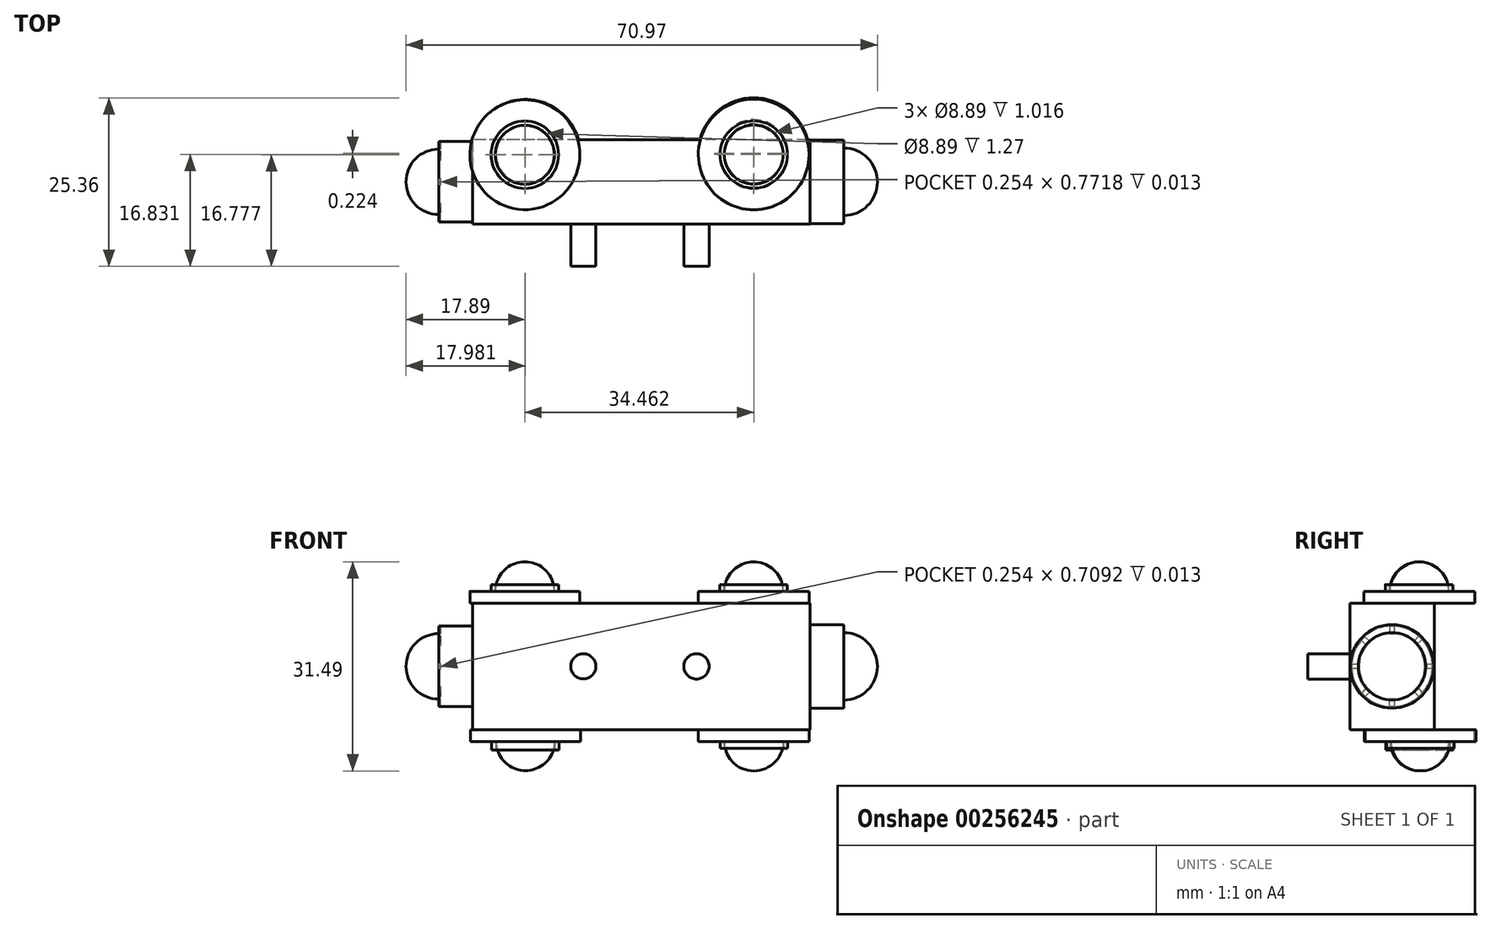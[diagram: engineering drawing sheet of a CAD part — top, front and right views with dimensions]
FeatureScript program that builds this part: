
annotation { "Feature Type Name" : "Feature", "Feature Type Description" : "" }
export const myFeature = defineFeature(function(context is Context, id is Id, definition is map)
    precondition{}
    {
        {
            var Q0;
            Q0=qCreatedBy(makeId("Front.planeOp"),FACE);
            var sketch = newSketch(context, id + "F0", { "sketchPlane" : qUnion([Q0])});
            skLineSegment(sketch, "E0.bottom", {"start": v(25.4, 9.53) * mm, "end": v(-25.4, 9.53) * mm});
            skLineSegment(sketch, "E0.top", {"start": v(25.4, -9.52) * mm, "end": v(-25.4, -9.52) * mm});
            skLineSegment(sketch, "E0.left", {"start": v(25.4, 9.53) * mm, "end": v(25.4, -9.53) * mm});
            skLineSegment(sketch, "E0.right", {"start": v(-25.4, 9.53) * mm, "end": v(-25.4, -9.52) * mm});
            skPoint(sketch, "E0.middle", {"position": v(0, 0) * mm});
            skSolve(sketch);
        }
        {
            var Q0;
            Q0 = qSketchRegion(id + "F0", true);
            extrude(context, id + "F1", {"entities" : qUnion([Q0]), "endBound" : BoundingType.SYMMETRIC, "depth" : 12.7 * mm});
        }
        {
            var Q0;
            Q0=makeQuery(id+"F1.opExtrude","CAP_FACE",FACE,{"disambiguationData":[OSD([sQuery(id+"F0.wireOp",EDGE,"E0.bottom"),sQuery(id+"F0.wireOp",EDGE,"E0.top"),sQuery(id+"F0.wireOp",EDGE,"E0.left"),sQuery(id+"F0.wireOp",EDGE,"E0.right")])],"isStart":false});
            var sketch = newSketch(context, id + "F2", { "sketchPlane" : qUnion([Q0])});
            skCircle(sketch, "E1", {"center": v(-8.72, 0) * mm, "radius": 1.89 * mm});
            skSolve(sketch);
        }
        {
            var Q0;
            Q0 = qSketchRegion(id + "F2", true);
            extrude(context, id + "F3", {"entities" : qUnion([Q0]), "operationType" : NewBodyOperationType.ADD, "depth" : 6.35 * mm});
        }
        {
            var Q0;
            Q0=makeQuery(id+"F1.opExtrude","CAP_FACE",FACE,{"disambiguationData":[OSD([sQuery(id+"F0.wireOp",EDGE,"E0.bottom"),sQuery(id+"F0.wireOp",EDGE,"E0.top"),sQuery(id+"F0.wireOp",EDGE,"E0.left"),sQuery(id+"F0.wireOp",EDGE,"E0.right")])],"isStart":false});
            var sketch = newSketch(context, id + "F4", { "sketchPlane" : qUnion([Q0])});
            skCircle(sketch, "E2", {"center": v(8.31, 0) * mm, "radius": 1.9 * mm});
            skSolve(sketch);
        }
        {
            var Q0;
            Q0 = qSketchRegion(id + "F4", true);
            extrude(context, id + "F5", {"entities" : qUnion([Q0]), "operationType" : NewBodyOperationType.ADD, "depth" : 6.35 * mm});
        }
        {
            var Q0;
            Q0=makeQuery(id+"F1.opExtrude","SWEPT_FACE",FACE,{"disambiguationData":[OSD([sQuery(id+"F0.wireOp",EDGE,"E0.left")])]});
            var sketch = newSketch(context, id + "F6", { "sketchPlane" : qUnion([Q0])});
            skCircle(sketch, "E3", {"center": v(0, 0) * mm, "radius": 6.28 * mm});
            skSolve(sketch);
        }
        {
            var Q0;
            Q0 = qSketchRegion(id + "F6", true);
            extrude(context, id + "F7", {"entities" : qUnion([Q0]), "operationType" : NewBodyOperationType.ADD, "depth" : 5.08 * mm});
        }
        {
            var Q0;
            Q0=makeQuery(id+"F7.opExtrude","CAP_FACE",FACE,{"disambiguationData":[OSD([sQuery(id+"F6.wireOp",EDGE,"E3")])],"isStart":false});
            var sketch = newSketch(context, id + "F8", { "sketchPlane" : qUnion([Q0])});
            skArc(sketch, "E4", {"start": v(5.08, 0) * mm, "mid": v(0, 5.08) * mm, "end": v(-5.08, 0) * mm});
            skLineSegment(sketch, "E5", {"start": v(-5.08, 0) * mm, "end": v(5.08, 0) * mm});
            skSolve(sketch);
        }
        {
            var Q0;
            Q0 = qSketchRegion(id + "F8", true);
            var Q1;
            Q1=sQuery(id+"F8.wireOp",EDGE,"E5");
            revolve(context, id + "F9", {"operationType" : NewBodyOperationType.ADD, "entities" : qUnion([Q0]), "axis" : qUnion([Q1]), "revolveType" : RevolveType.ONE_DIRECTION, "angle" : 180 * degree});
        }
        {
            var Q0;
            Q0=makeQuery(id+"F1.opExtrude","SWEPT_FACE",FACE,{"disambiguationData":[OSD([sQuery(id+"F0.wireOp",EDGE,"E0.right")])]});
            var sketch = newSketch(context, id + "F10", { "sketchPlane" : qUnion([Q0])});
            skCircle(sketch, "E6", {"center": v(0, 0) * mm, "radius": 6.07 * mm});
            skSolve(sketch);
        }
        {
            var Q0;
            Q0 = qSketchRegion(id + "F10", true);
            extrude(context, id + "F11", {"entities" : qUnion([Q0]), "operationType" : NewBodyOperationType.ADD, "depth" : 5.08 * mm});
        }
        {
            var Q0;
            Q0=makeQuery(id+"F11.opExtrude","CAP_FACE",FACE,{"disambiguationData":[OSD([sQuery(id+"F10.wireOp",EDGE,"E6")])],"isStart":false});
            var sketch = newSketch(context, id + "F12", { "sketchPlane" : qUnion([Q0])});
            skArc(sketch, "E7", {"start": v(-4.93, 0) * mm, "mid": v(0, -4.93) * mm, "end": v(4.93, 0) * mm});
            skLineSegment(sketch, "E8", {"start": v(4.93, 0) * mm, "end": v(-4.93, 0) * mm});
            skSolve(sketch);
        }
        {
            var Q0;
            Q0 = qSketchRegion(id + "F12", true);
            var Q1;
            Q1=sQuery(id+"F12.wireOp",EDGE,"E8");
            revolve(context, id + "F13", {"operationType" : NewBodyOperationType.ADD, "entities" : qUnion([Q0]), "axis" : qUnion([Q1]), "revolveType" : RevolveType.ONE_DIRECTION, "angle" : 180 * degree});
        }
        {
            var Q0;
            Q0=makeQuery(id+"F1.opExtrude","SWEPT_FACE",FACE,{"disambiguationData":[OSD([sQuery(id+"F0.wireOp",EDGE,"E0.top")])]});
            var sketch = newSketch(context, id + "F14", { "sketchPlane" : qUnion([Q0])});
            skCircle(sketch, "E9", {"center": v(-17.43, -4.13) * mm, "radius": 8.28 * mm});
            skSolve(sketch);
        }
        {
            var Q0;
            Q0 = qSketchRegion(id + "F14", true);
            extrude(context, id + "F15", {"entities" : qUnion([Q0]), "operationType" : NewBodyOperationType.ADD, "depth" : 1.78 * mm});
        }
        {
            var Q0;
            Q0=makeQuery(id+"F15.opExtrude","CAP_FACE",FACE,{"disambiguationData":[OSD([sQuery(id+"F14.wireOp",EDGE,"E9")])],"isStart":false});
            var sketch = newSketch(context, id + "F16", { "sketchPlane" : qUnion([Q0])});
            skCircle(sketch, "E10", {"center": v(-17.43, -4.13) * mm, "radius": 5.08 * mm});
            skSolve(sketch);
        }
        {
            var Q0;
            Q0 = qSketchRegion(id + "F16", true);
            extrude(context, id + "F17", {"entities" : qUnion([Q0]), "operationType" : NewBodyOperationType.ADD, "depth" : 1.27 * mm});
        }
        {
            var Q0;
            Q0=makeQuery(id+"F17.opExtrude","CAP_FACE",FACE,{"disambiguationData":[OSD([sQuery(id+"F16.wireOp",EDGE,"E10")])],"isStart":false});
            var sketch = newSketch(context, id + "F18", { "sketchPlane" : qUnion([Q0])});
            skCircle(sketch, "E11", {"center": v(-17.43, -4.13) * mm, "radius": 4.45 * mm});
            skSolve(sketch);
        }
        {
            var Q0;
            Q0 = qSketchRegion(id + "F18", true);
            extrude(context, id + "F19", {"entities" : qUnion([Q0]), "operationType" : NewBodyOperationType.REMOVE, "oppositeDirection" : true, "depth" : 1.27 * mm});
        }
        {
            var Q0;
            Q0=makeQuery(id+"F19.boolean.opBoolean","COPY",FACE,{"derivedFrom":makeQuery(id+"F19.opExtrude","CAP_FACE",FACE,{"disambiguationData":[OSD([sQuery(id+"F18.wireOp",EDGE,"E11")])],"isStart":false})});
            var sketch = newSketch(context, id + "F20", { "sketchPlane" : qUnion([Q0])});
            skArc(sketch, "E12", {"start": v(-17.43, -8.53) * mm, "mid": v(-13.03, -4.13) * mm, "end": v(-17.43, 0.27) * mm});
            skLineSegment(sketch, "E13", {"start": v(-17.43, -8.58) * mm, "end": v(-17.43, 0.31) * mm});
            skSolve(sketch);
        }
        {
            var Q0;
            Q0 = qSketchRegion(id + "F20", true);
            var Q1;
            Q1=sQuery(id+"F20.wireOp",EDGE,"E13");
            revolve(context, id + "F21", {"operationType" : NewBodyOperationType.ADD, "entities" : qUnion([Q0]), "axis" : qUnion([Q1]), "revolveType" : RevolveType.ONE_DIRECTION, "oppositeDirection" : true, "angle" : 180 * degree});
        }
        {
            var Q0;
            Q0=makeQuery(id+"F1.opExtrude","SWEPT_FACE",FACE,{"disambiguationData":[OSD([sQuery(id+"F0.wireOp",EDGE,"E0.top")])]});
            var sketch = newSketch(context, id + "F22", { "sketchPlane" : qUnion([Q0])});
            skCircle(sketch, "E14", {"center": v(16.94, -4.3) * mm, "radius": 8.36 * mm});
            skSolve(sketch);
        }
        {
            var Q0;
            Q0 = qSketchRegion(id + "F22", true);
            extrude(context, id + "F23", {"entities" : qUnion([Q0]), "operationType" : NewBodyOperationType.ADD, "depth" : 1.78 * mm});
        }
        {
            var Q0;
            Q0=makeQuery(id+"F23.opExtrude","CAP_FACE",FACE,{"disambiguationData":[OSD([sQuery(id+"F22.wireOp",EDGE,"E14")])],"isStart":false});
            var sketch = newSketch(context, id + "F24", { "sketchPlane" : qUnion([Q0])});
            skCircle(sketch, "E15", {"center": v(16.94, -4.3) * mm, "radius": 5.08 * mm});
            skSolve(sketch);
        }
        {
            var Q0;
            Q0 = qSketchRegion(id + "F24", true);
            extrude(context, id + "F25", {"entities" : qUnion([Q0]), "operationType" : NewBodyOperationType.ADD, "depth" : 1.02 * mm});
        }
        {
            var Q0;
            Q0=makeQuery(id+"F25.opExtrude","CAP_FACE",FACE,{"disambiguationData":[OSD([sQuery(id+"F24.wireOp",EDGE,"E15")])],"isStart":false});
            var sketch = newSketch(context, id + "F26", { "sketchPlane" : qUnion([Q0])});
            skCircle(sketch, "E16", {"center": v(16.94, -4.3) * mm, "radius": 4.45 * mm});
            skSolve(sketch);
        }
        {
            var Q0;
            Q0 = qSketchRegion(id + "F26", true);
            extrude(context, id + "F27", {"entities" : qUnion([Q0]), "operationType" : NewBodyOperationType.REMOVE, "oppositeDirection" : true, "depth" : 1.02 * mm});
        }
        {
            var Q0;
            Q0=makeQuery(id+"F27.boolean.opBoolean","COPY",FACE,{"derivedFrom":makeQuery(id+"F27.opExtrude","CAP_FACE",FACE,{"disambiguationData":[OSD([sQuery(id+"F26.wireOp",EDGE,"E16")])],"isStart":false})});
            var sketch = newSketch(context, id + "F28", { "sketchPlane" : qUnion([Q0])});
            skArc(sketch, "E17", {"start": v(16.95, -8.75) * mm, "mid": v(21.39, -4.3) * mm, "end": v(16.95, 0.14) * mm});
            skLineSegment(sketch, "E18", {"start": v(16.95, 0.14) * mm, "end": v(16.95, -8.75) * mm});
            skSolve(sketch);
        }
        {
            var Q0;
            Q0 = qSketchRegion(id + "F28", true);
            var Q1;
            Q1=sQuery(id+"F28.wireOp",EDGE,"E18");
            revolve(context, id + "F29", {"operationType" : NewBodyOperationType.ADD, "entities" : qUnion([Q0]), "axis" : qUnion([Q1]), "revolveType" : RevolveType.ONE_DIRECTION, "angle" : 180 * degree});
        }
        {
            var Q0;
            Q0=makeQuery(id+"F1.opExtrude","SWEPT_FACE",FACE,{"disambiguationData":[OSD([sQuery(id+"F0.wireOp",EDGE,"E0.bottom")])]});
            var sketch = newSketch(context, id + "F30", { "sketchPlane" : qUnion([Q0])});
            skCircle(sketch, "E19", {"center": v(16.93, 4.11) * mm, "radius": 8.33 * mm});
            skSolve(sketch);
        }
        {
            var Q0;
            Q0 = qSketchRegion(id + "F30", true);
            extrude(context, id + "F31", {"entities" : qUnion([Q0]), "operationType" : NewBodyOperationType.ADD, "depth" : 1.78 * mm});
        }
        {
            var Q0;
            Q0=makeQuery(id+"F31.opExtrude","CAP_FACE",FACE,{"disambiguationData":[OSD([sQuery(id+"F30.wireOp",EDGE,"E19")])],"isStart":false});
            var sketch = newSketch(context, id + "F32", { "sketchPlane" : qUnion([Q0])});
            skCircle(sketch, "E20", {"center": v(16.93, 4.11) * mm, "radius": 5.08 * mm});
            skSolve(sketch);
        }
        {
            var Q0;
            Q0 = qSketchRegion(id + "F32", true);
            extrude(context, id + "F33", {"entities" : qUnion([Q0]), "operationType" : NewBodyOperationType.ADD, "depth" : 1.02 * mm});
        }
        {
            var Q0;
            Q0=makeQuery(id+"F33.opExtrude","CAP_FACE",FACE,{"disambiguationData":[OSD([sQuery(id+"F32.wireOp",EDGE,"E20")])],"isStart":false});
            var sketch = newSketch(context, id + "F34", { "sketchPlane" : qUnion([Q0])});
            skCircle(sketch, "E21", {"center": v(16.93, 4.11) * mm, "radius": 4.44 * mm});
            skSolve(sketch);
        }
        {
            var Q0;
            Q0 = qSketchRegion(id + "F34", true);
            extrude(context, id + "F35", {"entities" : qUnion([Q0]), "operationType" : NewBodyOperationType.REMOVE, "oppositeDirection" : true, "depth" : 1.02 * mm});
        }
        {
            var Q0;
            Q0=makeQuery(id+"F35.boolean.opBoolean","COPY",FACE,{"derivedFrom":makeQuery(id+"F35.opExtrude","CAP_FACE",FACE,{"disambiguationData":[OSD([sQuery(id+"F34.wireOp",EDGE,"E21")])],"isStart":false})});
            var sketch = newSketch(context, id + "F36", { "sketchPlane" : qUnion([Q0])});
            skArc(sketch, "E22", {"start": v(16.93, 8.54) * mm, "mid": v(12.5, 4.11) * mm, "end": v(16.93, -0.32) * mm});
            skLineSegment(sketch, "E23", {"start": v(16.93, 8.56) * mm, "end": v(16.93, -0.33) * mm});
            skSolve(sketch);
        }
        {
            var Q0;
            Q0 = qSketchRegion(id + "F36", true);
            var Q1;
            Q1=sQuery(id+"F36.wireOp",EDGE,"E23");
            revolve(context, id + "F37", {"operationType" : NewBodyOperationType.ADD, "entities" : qUnion([Q0]), "axis" : qUnion([Q1]), "revolveType" : RevolveType.ONE_DIRECTION, "oppositeDirection" : true, "angle" : 180 * degree});
        }
        {
            var Q0;
            Q0=makeQuery(id+"F1.opExtrude","SWEPT_FACE",FACE,{"disambiguationData":[OSD([sQuery(id+"F0.wireOp",EDGE,"E0.bottom")])]});
            var sketch = newSketch(context, id + "F38", { "sketchPlane" : qUnion([Q0])});
            skCircle(sketch, "E24", {"center": v(-17.52, 4.08) * mm, "radius": 8.26 * mm});
            skSolve(sketch);
        }
        {
            var Q0;
            Q0 = qSketchRegion(id + "F38", true);
            extrude(context, id + "F39", {"entities" : qUnion([Q0]), "operationType" : NewBodyOperationType.ADD, "depth" : 1.78 * mm});
        }
        {
            var Q0;
            Q0=makeQuery(id+"F39.opExtrude","CAP_FACE",FACE,{"disambiguationData":[OSD([sQuery(id+"F38.wireOp",EDGE,"E24")])],"isStart":false});
            var sketch = newSketch(context, id + "F40", { "sketchPlane" : qUnion([Q0])});
            skCircle(sketch, "E25", {"center": v(-17.52, 4.08) * mm, "radius": 5.08 * mm});
            skSolve(sketch);
        }
        {
            var Q0;
            Q0 = qSketchRegion(id + "F40", true);
            extrude(context, id + "F41", {"entities" : qUnion([Q0]), "operationType" : NewBodyOperationType.ADD, "depth" : 1.02 * mm});
        }
        {
            var Q0;
            Q0=makeQuery(id+"F41.opExtrude","CAP_FACE",FACE,{"disambiguationData":[OSD([sQuery(id+"F40.wireOp",EDGE,"E25")])],"isStart":false});
            var sketch = newSketch(context, id + "F42", { "sketchPlane" : qUnion([Q0])});
            skCircle(sketch, "E26", {"center": v(-17.52, 4.08) * mm, "radius": 4.45 * mm});
            skSolve(sketch);
        }
        {
            var Q0;
            Q0 = qSketchRegion(id + "F42", true);
            extrude(context, id + "F43", {"entities" : qUnion([Q0]), "operationType" : NewBodyOperationType.REMOVE, "oppositeDirection" : true, "depth" : 1.02 * mm});
        }
        {
            var Q0;
            Q0=makeQuery(id+"F43.boolean.opBoolean","COPY",FACE,{"derivedFrom":makeQuery(id+"F43.opExtrude","CAP_FACE",FACE,{"disambiguationData":[OSD([sQuery(id+"F42.wireOp",EDGE,"E26")])],"isStart":false})});
            var sketch = newSketch(context, id + "F44", { "sketchPlane" : qUnion([Q0])});
            skArc(sketch, "E27", {"start": v(-17.52, 8.52) * mm, "mid": v(-21.96, 4.08) * mm, "end": v(-17.52, -0.36) * mm});
            skLineSegment(sketch, "E28", {"start": v(-17.52, -0.37) * mm, "end": v(-17.52, 8.52) * mm});
            skSolve(sketch);
        }
        {
            var Q0;
            Q0 = qSketchRegion(id + "F44", true);
            var Q1;
            Q1=sQuery(id+"F44.wireOp",EDGE,"E28");
            revolve(context, id + "F45", {"operationType" : NewBodyOperationType.ADD, "entities" : qUnion([Q0]), "axis" : qUnion([Q1]), "revolveType" : RevolveType.ONE_DIRECTION, "angle" : 180 * degree});
        }
        {
            var Q0;
            Q0=makeQuery(id+"F11.opExtrude","CAP_FACE",FACE,{"disambiguationData":[OSD([sQuery(id+"F10.wireOp",EDGE,"E6")])],"isStart":false});
            var sketch = newSketch(context, id + "F46", { "sketchPlane" : qUnion([Q0])});
            skLineSegment(sketch, "E29", {"start": v(6.06, 0.35) * mm, "end": v(4.91, 0.35) * mm});
            skLineSegment(sketch, "E30", {"start": v(4.91, 0.35) * mm, "end": v(4.91, -0.35) * mm});
            skLineSegment(sketch, "E31", {"start": v(4.91, -0.35) * mm, "end": v(6.06, -0.35) * mm});
            skLineSegment(sketch, "E32", {"start": v(6.06, -0.35) * mm, "end": v(6.06, 0.35) * mm});
            skSolve(sketch);
        }
        {
            var Q0;
            Q0 = qSketchRegion(id + "F46", true);
            extrude(context, id + "F47", {"entities" : qUnion([Q0]), "operationType" : NewBodyOperationType.REMOVE, "oppositeDirection" : true, "depth" : 0.25 * mm});
        }
        {
            var Q0;
            {var subQ3=sQuery(id+"F10.wireOp",EDGE,"E6");Q0=makeQuery(id+"F47.boolean.opBoolean","SPLIT",FACE,{"disambiguationData":[TD([makeQuery(id+"F13.opRevolve","SWEPT_FACE",FACE,{"disambiguationData":[OSD([sQuery(id+"F12.wireOp",EDGE,"E7")])]})])],"derivedFrom":makeQuery(id+"F11.opExtrude","CAP_FACE",FACE,{"disambiguationData":[OSD([subQ3])],"isStart":false})});}
            var sketch = newSketch(context, id + "F48", { "sketchPlane" : qUnion([Q0])});
            skLineSegment(sketch, "E33", {"start": v(-4.91, 0.35) * mm, "end": v(-6.06, 0.35) * mm});
            skLineSegment(sketch, "E34", {"start": v(-6.06, 0.35) * mm, "end": v(-6.1, -0.35) * mm});
            skLineSegment(sketch, "E35", {"start": v(-6.1, -0.35) * mm, "end": v(-4.91, -0.35) * mm});
            skLineSegment(sketch, "E36", {"start": v(-4.91, -0.35) * mm, "end": v(-4.91, 0.35) * mm});
            skSolve(sketch);
        }
        {
            var Q0;
            Q0 = qSketchRegion(id + "F48", true);
            extrude(context, id + "F49", {"entities" : qUnion([Q0]), "operationType" : NewBodyOperationType.REMOVE, "oppositeDirection" : true, "depth" : 0.25 * mm});
        }
        {
            var Q0;
            {var subQ2=sQuery(id+"F46.wireOp",EDGE,"E29");var subQ4=makeQuery(id+"F47.opExtrude","SWEPT_FACE",FACE,{"disambiguationData":[OSD([subQ2])]});var subQ5=makeQuery(id+"F13.opRevolve","SWEPT_FACE",FACE,{"disambiguationData":[OSD([sQuery(id+"F12.wireOp",EDGE,"E7")])]});var subQ6=sQuery(id+"F10.wireOp",EDGE,"E6");Q0=makeQuery(id+"F49.boolean.opBoolean","SPLIT",FACE,{"disambiguationData":[TD([makeQuery(id+"F47.boolean.opBoolean","COPY",FACE,{"derivedFrom":subQ4})])],"derivedFrom":makeQuery(id+"F47.boolean.opBoolean","SPLIT",FACE,{"disambiguationData":[TD([subQ5])],"derivedFrom":makeQuery(id+"F11.opExtrude","CAP_FACE",FACE,{"disambiguationData":[OSD([subQ6])],"isStart":false})})});}
            var sketch = newSketch(context, id + "F50", { "sketchPlane" : qUnion([Q0])});
            skLineSegment(sketch, "E37", {"start": v(-0.39, 4.91) * mm, "end": v(-0.39, 6.06) * mm});
            skLineSegment(sketch, "E38", {"start": v(-0.39, 6.06) * mm, "end": v(0.39, 6.06) * mm});
            skLineSegment(sketch, "E39", {"start": v(0.39, 6.06) * mm, "end": v(0.39, 4.91) * mm});
            skLineSegment(sketch, "E40", {"start": v(0.39, 4.91) * mm, "end": v(-0.39, 4.91) * mm});
            skSolve(sketch);
        }
        {
            var Q0;
            Q0 = qSketchRegion(id + "F50", true);
            extrude(context, id + "F51", {"entities" : qUnion([Q0]), "operationType" : NewBodyOperationType.REMOVE, "oppositeDirection" : true, "depth" : 0.25 * mm});
        }
        {
            var Q0;
            {var subQ2=sQuery(id+"F10.wireOp",EDGE,"E6");var subQ4=sQuery(id+"F46.wireOp",EDGE,"E31");var subQ7=makeQuery(id+"F13.opRevolve","SWEPT_FACE",FACE,{"disambiguationData":[OSD([sQuery(id+"F12.wireOp",EDGE,"E7")])]});var subQ8=makeQuery(id+"F47.opExtrude","SWEPT_FACE",FACE,{"disambiguationData":[OSD([subQ4])]});Q0=makeQuery(id+"F49.boolean.opBoolean","SPLIT",FACE,{"disambiguationData":[TD([makeQuery(id+"F47.boolean.opBoolean","COPY",FACE,{"derivedFrom":subQ8})])],"derivedFrom":makeQuery(id+"F47.boolean.opBoolean","SPLIT",FACE,{"disambiguationData":[TD([subQ7])],"derivedFrom":makeQuery(id+"F11.opExtrude","CAP_FACE",FACE,{"disambiguationData":[OSD([subQ2])],"isStart":false})})});}
            var sketch = newSketch(context, id + "F52", { "sketchPlane" : qUnion([Q0])});
            skLineSegment(sketch, "E41", {"start": v(0.42, -4.9) * mm, "end": v(0.42, -6.05) * mm});
            skLineSegment(sketch, "E42", {"start": v(0.42, -6.05) * mm, "end": v(-0.42, -6.05) * mm});
            skLineSegment(sketch, "E43", {"start": v(-0.42, -6.05) * mm, "end": v(-0.42, -4.9) * mm});
            skLineSegment(sketch, "E44", {"start": v(-0.42, -4.9) * mm, "end": v(0.42, -4.9) * mm});
            skSolve(sketch);
        }
        {
            var Q0;
            Q0 = qSketchRegion(id + "F52", true);
            extrude(context, id + "F53", {"entities" : qUnion([Q0]), "operationType" : NewBodyOperationType.REMOVE, "oppositeDirection" : true, "depth" : 0.25 * mm});
        }
        {
            var Q0;
            {var subQ0=sQuery(id+"F46.wireOp",EDGE,"E30");var subQ1=makeQuery(id+"F47.opExtrude","SWEPT_FACE",FACE,{"disambiguationData":[OSD([subQ0])]});var subQ2=makeQuery(id+"F47.boolean.opBoolean","COPY",FACE,{"derivedFrom":subQ1});var subQ3=sQuery(id+"F10.wireOp",EDGE,"E6");var subQ5=sQuery(id+"F46.wireOp",EDGE,"E31");var subQ9=makeQuery(id+"F13.opRevolve","SWEPT_FACE",FACE,{"disambiguationData":[OSD([sQuery(id+"F12.wireOp",EDGE,"E7")])]});var subQ11=makeQuery(id+"F47.opExtrude","SWEPT_FACE",FACE,{"disambiguationData":[OSD([subQ5])]});var subQ12=makeQuery(id+"F47.boolean.opBoolean","COPY",FACE,{"derivedFrom":subQ11});Q0=makeQuery(id+"F53.boolean.opBoolean","SPLIT",FACE,{"disambiguationData":[TD([subQ2])],"derivedFrom":makeQuery(id+"F49.boolean.opBoolean","SPLIT",FACE,{"disambiguationData":[TD([subQ12])],"derivedFrom":makeQuery(id+"F47.boolean.opBoolean","SPLIT",FACE,{"disambiguationData":[TD([subQ9])],"derivedFrom":makeQuery(id+"F11.opExtrude","CAP_FACE",FACE,{"disambiguationData":[OSD([subQ3])],"isStart":false})})})});}
            var sketch = newSketch(context, id + "F54", { "sketchPlane" : qUnion([Q0])});
            skLineSegment(sketch, "E45", {"start": v(3.8, -3.14) * mm, "end": v(4.57, -4) * mm});
            skLineSegment(sketch, "E46", {"start": v(4.57, -4) * mm, "end": v(4.01, -4.55) * mm});
            skLineSegment(sketch, "E47", {"start": v(4.01, -4.55) * mm, "end": v(3.22, -3.73) * mm});
            skLineSegment(sketch, "E48", {"start": v(3.22, -3.73) * mm, "end": v(3.8, -3.14) * mm});
            skSolve(sketch);
        }
        {
            var Q0;
            Q0 = qSketchRegion(id + "F54", true);
            extrude(context, id + "F55", {"entities" : qUnion([Q0]), "operationType" : NewBodyOperationType.REMOVE, "oppositeDirection" : true, "depth" : 0.25 * mm});
        }
        {
            var Q0;
            {var subQ0=makeQuery(id+"F13.opRevolve","SWEPT_FACE",FACE,{"disambiguationData":[OSD([sQuery(id+"F12.wireOp",EDGE,"E7")])]});var subQ2=sQuery(id+"F48.wireOp",EDGE,"E35");var subQ3=makeQuery(id+"F49.opExtrude","SWEPT_FACE",FACE,{"disambiguationData":[OSD([subQ2])]});var subQ6=sQuery(id+"F10.wireOp",EDGE,"E6");var subQ12=sQuery(id+"F46.wireOp",EDGE,"E31");var subQ15=makeQuery(id+"F47.opExtrude","SWEPT_FACE",FACE,{"disambiguationData":[OSD([subQ12])]});Q0=makeQuery(id+"F53.boolean.opBoolean","SPLIT",FACE,{"disambiguationData":[TD([makeQuery(id+"F49.boolean.opBoolean","COPY",FACE,{"derivedFrom":subQ3})])],"derivedFrom":makeQuery(id+"F49.boolean.opBoolean","SPLIT",FACE,{"disambiguationData":[TD([makeQuery(id+"F47.boolean.opBoolean","COPY",FACE,{"derivedFrom":subQ15})])],"derivedFrom":makeQuery(id+"F47.boolean.opBoolean","SPLIT",FACE,{"disambiguationData":[TD([subQ0])],"derivedFrom":makeQuery(id+"F11.opExtrude","CAP_FACE",FACE,{"disambiguationData":[OSD([subQ6])],"isStart":false})})})});}
            var sketch = newSketch(context, id + "F56", { "sketchPlane" : qUnion([Q0])});
            skLineSegment(sketch, "E49", {"start": v(-3.28, -3.68) * mm, "end": v(-4.01, -4.55) * mm});
            skLineSegment(sketch, "E50", {"start": v(-4.01, -4.55) * mm, "end": v(-4.6, -3.96) * mm});
            skLineSegment(sketch, "E51", {"start": v(-4.6, -3.96) * mm, "end": v(-3.83, -3.1) * mm});
            skLineSegment(sketch, "E52", {"start": v(-3.83, -3.1) * mm, "end": v(-3.28, -3.68) * mm});
            skSolve(sketch);
        }
        {
            var Q0;
            Q0 = qSketchRegion(id + "F56", true);
            extrude(context, id + "F57", {"entities" : qUnion([Q0]), "operationType" : NewBodyOperationType.REMOVE, "oppositeDirection" : true, "depth" : 0.25 * mm});
        }
        {
            var Q0;
            {var subQ2=sQuery(id+"F46.wireOp",EDGE,"E29");var subQ5=makeQuery(id+"F47.opExtrude","SWEPT_FACE",FACE,{"disambiguationData":[OSD([subQ2])]});var subQ6=makeQuery(id+"F47.boolean.opBoolean","COPY",FACE,{"derivedFrom":subQ5});var subQ7=makeQuery(id+"F13.opRevolve","SWEPT_FACE",FACE,{"disambiguationData":[OSD([sQuery(id+"F12.wireOp",EDGE,"E7")])]});var subQ10=sQuery(id+"F10.wireOp",EDGE,"E6");Q0=makeQuery(id+"F51.boolean.opBoolean","SPLIT",FACE,{"disambiguationData":[TD([subQ6])],"derivedFrom":makeQuery(id+"F49.boolean.opBoolean","SPLIT",FACE,{"disambiguationData":[TD([subQ6])],"derivedFrom":makeQuery(id+"F47.boolean.opBoolean","SPLIT",FACE,{"disambiguationData":[TD([subQ7])],"derivedFrom":makeQuery(id+"F11.opExtrude","CAP_FACE",FACE,{"disambiguationData":[OSD([subQ10])],"isStart":false})})})});}
            var sketch = newSketch(context, id + "F58", { "sketchPlane" : qUnion([Q0])});
            skLineSegment(sketch, "E53", {"start": v(3.78, 3.17) * mm, "end": v(4.62, 3.93) * mm});
            skLineSegment(sketch, "E54", {"start": v(4.62, 3.93) * mm, "end": v(4.1, 4.47) * mm});
            skLineSegment(sketch, "E55", {"start": v(4.1, 4.47) * mm, "end": v(3.26, 3.7) * mm});
            skLineSegment(sketch, "E56", {"start": v(3.26, 3.7) * mm, "end": v(3.78, 3.17) * mm});
            skSolve(sketch);
        }
        {
            var Q0;
            Q0 = qSketchRegion(id + "F58", true);
            extrude(context, id + "F59", {"entities" : qUnion([Q0]), "operationType" : NewBodyOperationType.REMOVE, "oppositeDirection" : true, "depth" : 0.25 * mm});
        }
        {
            var Q0;
            {var subQ0=makeQuery(id+"F13.opRevolve","SWEPT_FACE",FACE,{"disambiguationData":[OSD([sQuery(id+"F12.wireOp",EDGE,"E7")])]});var subQ4=sQuery(id+"F48.wireOp",EDGE,"E33");var subQ6=makeQuery(id+"F49.opExtrude","SWEPT_FACE",FACE,{"disambiguationData":[OSD([subQ4])]});var subQ7=sQuery(id+"F10.wireOp",EDGE,"E6");var subQ12=sQuery(id+"F46.wireOp",EDGE,"E29");var subQ14=makeQuery(id+"F47.opExtrude","SWEPT_FACE",FACE,{"disambiguationData":[OSD([subQ12])]});Q0=makeQuery(id+"F51.boolean.opBoolean","SPLIT",FACE,{"disambiguationData":[TD([makeQuery(id+"F49.boolean.opBoolean","COPY",FACE,{"derivedFrom":subQ6})])],"derivedFrom":makeQuery(id+"F49.boolean.opBoolean","SPLIT",FACE,{"disambiguationData":[TD([makeQuery(id+"F47.boolean.opBoolean","COPY",FACE,{"derivedFrom":subQ14})])],"derivedFrom":makeQuery(id+"F47.boolean.opBoolean","SPLIT",FACE,{"disambiguationData":[TD([subQ0])],"derivedFrom":makeQuery(id+"F11.opExtrude","CAP_FACE",FACE,{"disambiguationData":[OSD([subQ7])],"isStart":false})})})});}
            var sketch = newSketch(context, id + "F60", { "sketchPlane" : qUnion([Q0])});
            skLineSegment(sketch, "E57", {"start": v(-3.24, 3.72) * mm, "end": v(-4.04, 4.52) * mm});
            skLineSegment(sketch, "E58", {"start": v(-4.04, 4.52) * mm, "end": v(-4.53, 4.04) * mm});
            skLineSegment(sketch, "E59", {"start": v(-4.53, 4.04) * mm, "end": v(-3.7, 3.25) * mm});
            skLineSegment(sketch, "E60", {"start": v(-3.7, 3.25) * mm, "end": v(-3.24, 3.72) * mm});
            skSolve(sketch);
        }
        {
            var Q0;
            Q0 = qSketchRegion(id + "F60", true);
            extrude(context, id + "F61", {"entities" : qUnion([Q0]), "operationType" : NewBodyOperationType.REMOVE, "oppositeDirection" : true, "depth" : 0.25 * mm});
        }
    });
